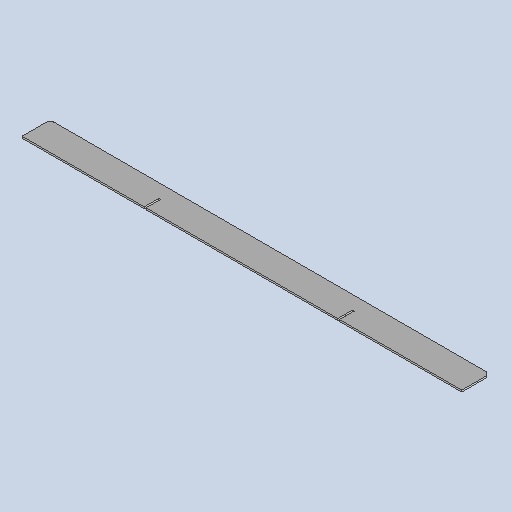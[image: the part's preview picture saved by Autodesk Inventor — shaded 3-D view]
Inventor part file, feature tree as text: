
AUTODESK INVENTOR PART (.ipt)
format: ipt  version: 2025 (Build 290162010, 162A)  size: 372,736 bytes
history: native  units: mm
features: other x5, sketch x3, sheet_metal_op x1, extrude x1
ambient origin geometry x8: Origin, YZ Plane, XZ Plane, XY Plane, X Axis, Y Axis, Z Axis, Center Point
bodies: Body1 (feature_tree)
feature tree (10):
  sheet_metal_op  "Face1"
  extrude  "Extrusion1"  Depth=780.0mm
  other  "Mark1"
  other  "A-Side Definition"
  other  "Corner Chamfer1"
  sketch  "Sketch1"  dims[d16=50.0mm d17=780.0mm]
  other  "Plate2"
  sketch  "Sketch2"  dims[d18=50.0mm]
  sketch  "Sketch4"  dims[d19=50.0mm d20=3.0mm d23=26.0mm d24=10.0mm d25=0.0mm d27=26.0mm d28=3.1mm d34=340.0mm d35=6.0mm d36=6.0mm d37=45.0deg]
  other  "Definition1"
